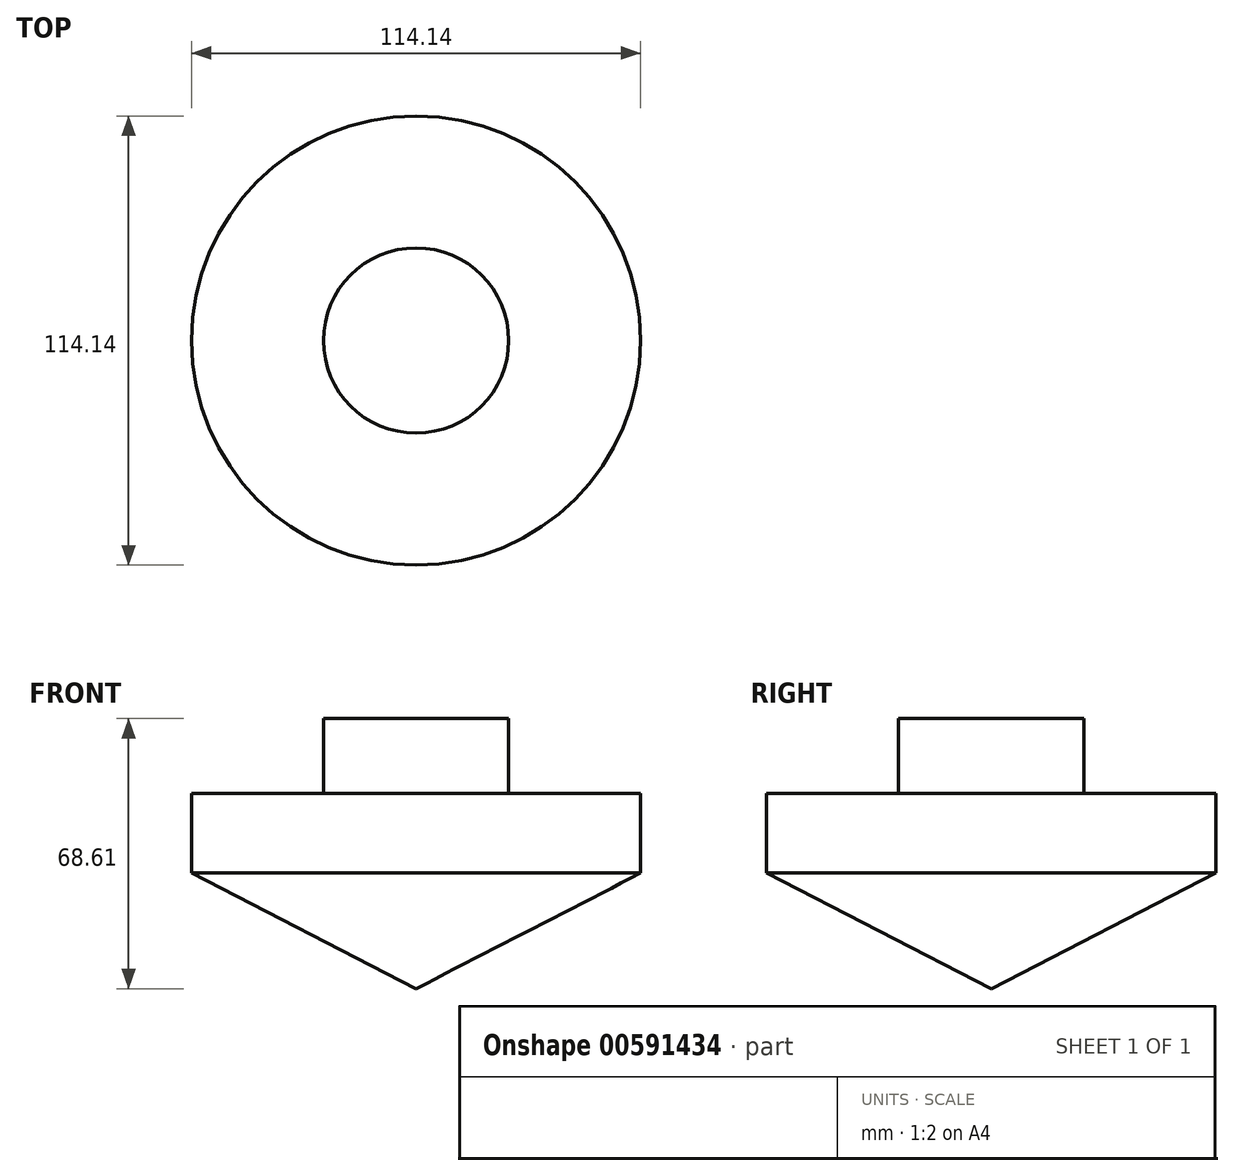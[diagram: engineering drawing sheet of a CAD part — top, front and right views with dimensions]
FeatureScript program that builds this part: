
annotation { "Feature Type Name" : "Feature", "Feature Type Description" : "" }
export const myFeature = defineFeature(function(context is Context, id is Id, definition is map)
    precondition{}
    {
        {
            var Q0;
            Q0=qCreatedBy(makeId("Front.planeOp"),FACE);
            var sketch = newSketch(context, id + "F0", { "sketchPlane" : qUnion([Q0])});
            skLineSegment(sketch, "E0", {"start": v(0, 0) * mm, "end": v(57.07, 29.37) * mm});
            skLineSegment(sketch, "E1", {"start": v(57.07, 29.37) * mm, "end": v(57.07, 49.56) * mm});
            skLineSegment(sketch, "E2", {"start": v(57.07, 49.56) * mm, "end": v(23.54, 49.56) * mm});
            skLineSegment(sketch, "E3", {"start": v(23.54, 49.56) * mm, "end": v(23.54, 68.61) * mm});
            skLineSegment(sketch, "E4", {"start": v(23.54, 68.61) * mm, "end": v(0, 68.61) * mm});
            skLineSegment(sketch, "E5", {"start": v(0, 68.61) * mm, "end": v(0, 0) * mm});
            skSolve(sketch);
        }
        {
            var Q0;
            Q0=makeQuery(id+"F0.imprint","IMPRINT",FACE,{"disambiguationData":[TD([[makeQuery(id+"F0.imprint","IMPRINT",EDGE,{"derivedFrom":sQuery(id+"F0.wireOp",EDGE,"E0")}),1.0]])]});
            var Q1;
            Q1=sQuery(id+"F0.wireOp",EDGE,"E5");
            revolve(context, id + "F1", {"entities" : qUnion([Q0]), "axis" : qUnion([Q1]), "revolveType" : RevolveType.FULL});
        }
    });
